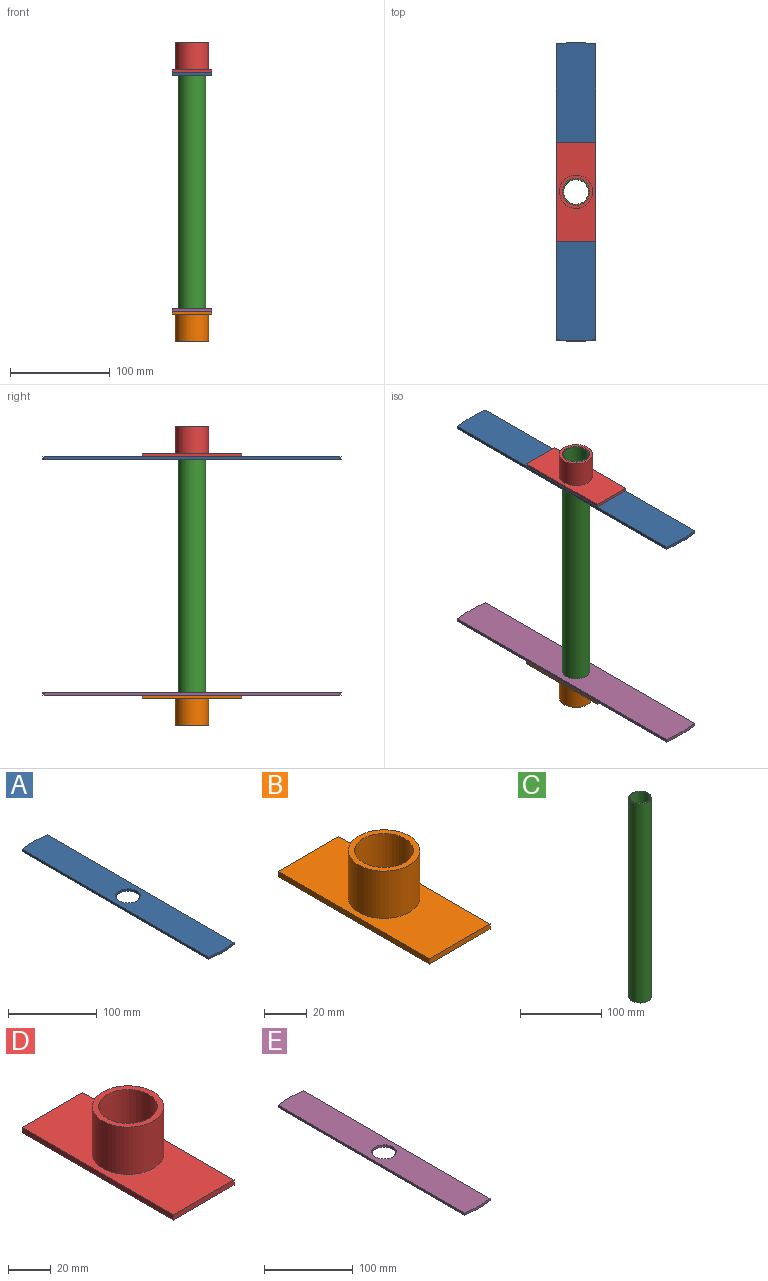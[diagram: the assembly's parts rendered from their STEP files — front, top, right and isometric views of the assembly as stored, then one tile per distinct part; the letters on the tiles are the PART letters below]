
ASSEMBLY  parts=5 mates=8
PART A: 7 faces, bbox 40x300x3 mm
  f0: plane 297.32x3mm, normal (-1,0,0), area 892mm2, adj f1,f3,f4,f5
  f1: cylinder r=150mm len=40mm, axis (0,0,-1), area 120.4mm2, adj f0,f2,f4,f5
  f2: plane 297.32x3mm, normal (1,0,0), area 892mm2, adj f1,f3,f4,f5
  f3: cylinder r=150mm len=40mm, axis (0,0,-1), area 120.4mm2, adj f0,f2,f4,f5
  f4: plane 300x40mm, normal (0,0,1), area 11374.7mm2, adj f0,f1,f2,f3,f6
  f5: plane 300x40mm, normal (0,0,-1), area 11374.7mm2, adj f0,f1,f2,f3,f6
  f6: cylinder r=13.7mm len=27.4mm, axis (0,0,-1), area 258.2mm2, adj f4,f5
PART B: 9 faces, bbox 40x100x30 mm
  f0: plane 40x3mm, normal (0,-1,0), area 120mm2, adj f1,f3,f4,f5
  f1: plane 100x3mm, normal (1,0,0), area 300mm2, adj f0,f2,f4,f5
  f2: plane 40x3mm, normal (0,1,0), area 120mm2, adj f1,f3,f4,f5
  f3: plane 100x3mm, normal (-1,0,0), area 300mm2, adj f0,f2,f4,f5
  f4: plane 100x40mm, normal (0,0,1), area 3123.8mm2, adj f0,f1,f2,f3,f6
  f5: plane 100x40mm, normal (0,0,-1), area 3410.4mm2, adj f0,f1,f2,f3,f8
  f6: cylinder r=16.7mm len=33.4mm, axis (0,0,-1), area 2833.1mm2, adj f4,f7
  f7: plane 33.4x33.4mm, normal (0,0,1), area 286.5mm2, adj f6,f8
  f8: cylinder r=13.7mm len=30mm, axis (0,0,-1), area 2582.4mm2, adj f5,f7
PART C: 4 faces, bbox 27.4x27.4x300 mm
  f0: cylinder r=13.7mm len=300mm, axis (0,0,-1), area 25823.9mm2, adj f1,f2
  f1: plane 27.4x27.4mm, normal (0,0,1), area 98.8mm2, adj f0,f3
  f2: plane 27.4x27.4mm, normal (0,0,-1), area 98.8mm2, adj f0,f3
  f3: cylinder r=12.5mm len=300mm, axis (0,0,-1), area 23561.9mm2, adj f1,f2
PART D: 9 faces, bbox 40x100x30 mm
  f0: plane 40x3mm, normal (0,-1,0), area 120mm2, adj f1,f3,f4,f5
  f1: plane 100x3mm, normal (1,0,0), area 300mm2, adj f0,f2,f4,f5
  f2: plane 40x3mm, normal (0,1,0), area 120mm2, adj f1,f3,f4,f5
  f3: plane 100x3mm, normal (-1,0,0), area 300mm2, adj f0,f2,f4,f5
  f4: plane 100x40mm, normal (0,0,1), area 3123.8mm2, adj f0,f1,f2,f3,f6
  f5: plane 100x40mm, normal (0,0,-1), area 3410.4mm2, adj f0,f1,f2,f3,f8
  f6: cylinder r=16.7mm len=33.4mm, axis (0,0,-1), area 2833.1mm2, adj f4,f7
  f7: plane 33.4x33.4mm, normal (0,0,1), area 286.5mm2, adj f6,f8
  f8: cylinder r=13.7mm len=30mm, axis (0,0,-1), area 2582.4mm2, adj f5,f7
PART E: 7 faces, bbox 40x300x3 mm
  f0: plane 297.32x3mm, normal (-1,0,0), area 892mm2, adj f1,f3,f4,f5
  f1: cylinder r=150mm len=40mm, axis (0,0,-1), area 120.4mm2, adj f0,f2,f4,f5
  f2: plane 297.32x3mm, normal (1,0,0), area 892mm2, adj f1,f3,f4,f5
  f3: cylinder r=150mm len=40mm, axis (0,0,-1), area 120.4mm2, adj f0,f2,f4,f5
  f4: plane 300x40mm, normal (0,0,1), area 11374.7mm2, adj f0,f1,f2,f3,f6
  f5: plane 300x40mm, normal (0,0,-1), area 11374.7mm2, adj f0,f1,f2,f3,f6
  f6: cylinder r=13.7mm len=27.4mm, axis (0,0,-1), area 258.2mm2, adj f4,f5
PLACE A t=(20,50,120)mm
PLACE B rot(axis=(1,0,0),180deg) t=(-125.84,146.82,-117)mm
PLACE C t=(116.76,81.8,-147)mm
PLACE D t=(-75.84,70.35,123)mm
PLACE E t=(70,50,-117)mm
MATE slider C.f0 <-> D.f6  axis (0,0,-1) through (85.32,108.58,3)mm
MATE planar B.f5 <-> E.f1  axis (0,0,1) through (85.32,58.58,-117)mm
MATE planar B.f6 <-> C.f0  axis (0,0,-1) through (85.32,108.58,-147)mm
MATE planar D.f5 <-> A.f1  axis (0,0,-1) through (65.32,108.58,123)mm
MATE slider C.f0 <-> B.f6  axis (0,0,-1) through (85.32,108.58,-147)mm
MATE planar D.f6 <-> C.f0  axis (0,0,1) through (85.32,108.58,153)mm
MATE slider C.f0 <-> E.f1  axis (0,0,-1) through (85.32,108.58,3)mm
MATE slider C.f0 <-> A.f1  axis (0,0,-1) through (85.32,108.58,3)mm
